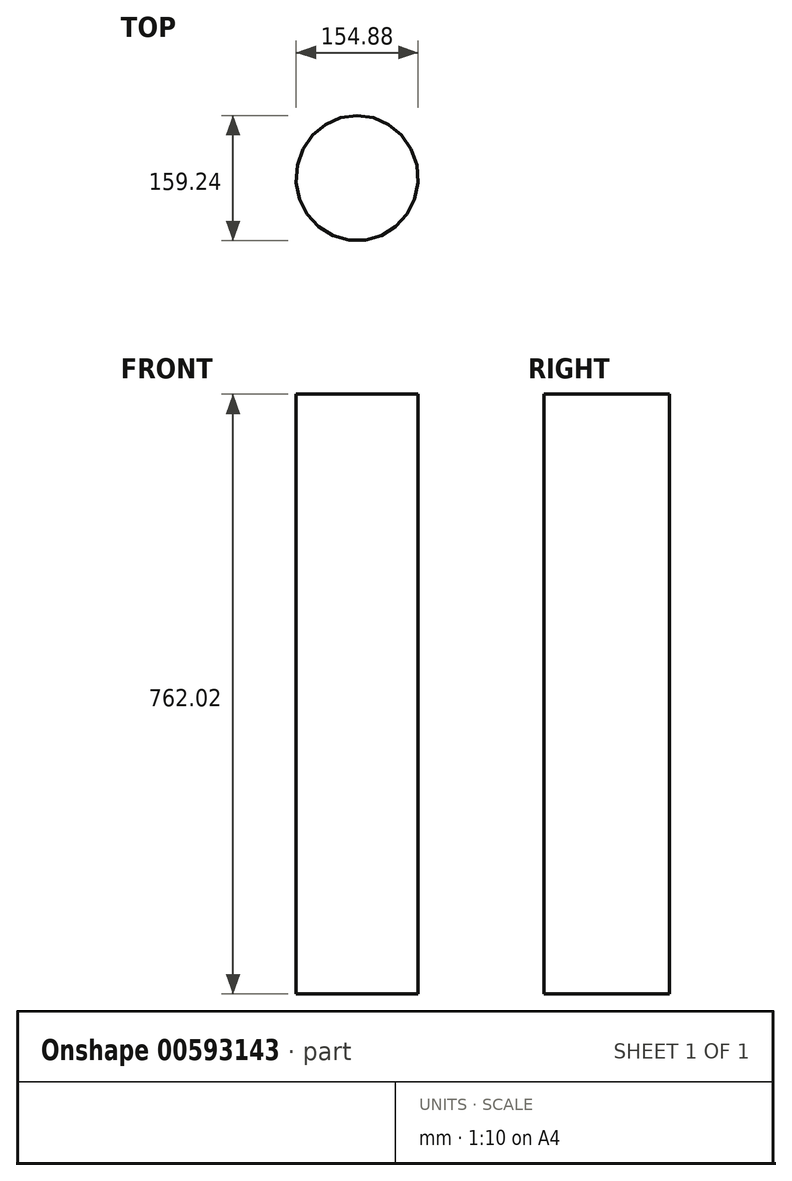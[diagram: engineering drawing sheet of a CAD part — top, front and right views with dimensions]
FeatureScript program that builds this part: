
annotation { "Feature Type Name" : "Feature", "Feature Type Description" : "" }
export const myFeature = defineFeature(function(context is Context, id is Id, definition is map)
    precondition{}
    {
        {
            var Q0;
            Q0=qCreatedBy(makeId("Top.planeOp"),FACE);
            var sketch = newSketch(context, id + "F0", { "sketchPlane" : qUnion([Q0])});
            skEllipse(sketch, "E0", {"center": v(0, 0) * mm, "majorRadius": 77.44 * mm, "minorRadius": 79.62 * mm, "majorAxis": v(1, 0)});
            skSolve(sketch);
        }
        {
            var Q0;
            Q0 = qSketchRegion(id + "F0", true);
            extrude(context, id + "F1", {"entities" : qUnion([Q0]), "depth" : 762 * mm, "offsetDistance" : 25.4 * mm, "hasSecondDirection" : true, "secondDirectionOppositeDirection" : true, "secondDirectionDepth" : 1 / 50.8 * mm});
        }
        {
            var Q0;
            Q0=makeQuery(id+"F1.opExtrude","CAP_FACE",FACE,{"disambiguationData":[OSD([sQuery(id+"F0.wireOp",EDGE,"E0")])],"isStart":false});
            var sketch = newSketch(context, id + "F2", { "sketchPlane" : qUnion([Q0])});
            skCircle(sketch, "E1", {"center": v(0, 0) * mm, "radius": 61.05 * mm});
            skSolve(sketch);
        }
        {
            var Q0;
            Q0 = qSketchRegion(id + "F2", true);
            extrude(context, id + "F3", {"entities" : qUnion([Q0]), "operationType" : NewBodyOperationType.ADD, "oppositeDirection" : true, "depth" : 736.6 * mm, "offsetDistance" : 25.4 * mm});
        }
    });
